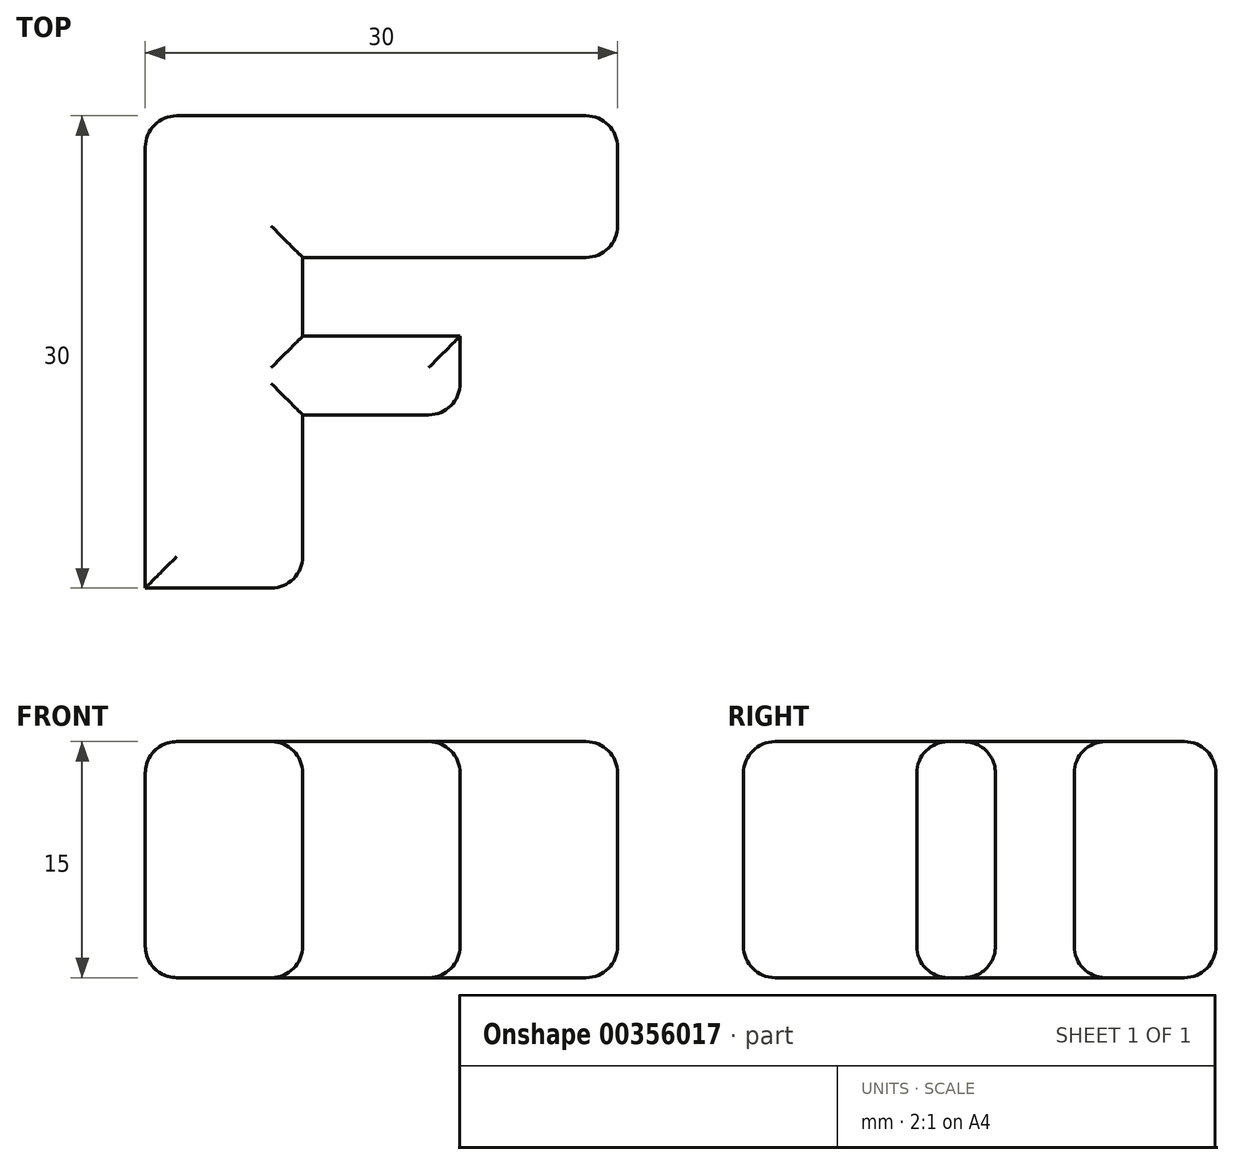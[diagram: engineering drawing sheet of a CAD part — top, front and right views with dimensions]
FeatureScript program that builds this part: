
annotation { "Feature Type Name" : "Feature", "Feature Type Description" : "" }
export const myFeature = defineFeature(function(context is Context, id is Id, definition is map)
    precondition{}
    {
        {
            var Q0;
            Q0=qCreatedBy(makeId("Top.planeOp"),FACE);
            var sketch = newSketch(context, id + "F0", { "sketchPlane" : qUnion([Q0])});
            skLineSegment(sketch, "E0", {"start": v(0, 0) * mm, "end": v(0, 30) * mm});
            skLineSegment(sketch, "E1", {"start": v(0, 30) * mm, "end": v(30, 30) * mm});
            skLineSegment(sketch, "E2", {"start": v(30, 30) * mm, "end": v(30, 21) * mm});
            skLineSegment(sketch, "E3", {"start": v(10, 21) * mm, "end": v(30, 21) * mm});
            skLineSegment(sketch, "E4", {"start": v(10, 21) * mm, "end": v(10, 16) * mm});
            skLineSegment(sketch, "E5", {"start": v(10, 16) * mm, "end": v(20, 16) * mm});
            skPoint(sketch, "E5.endSnap0", {"position": v(20, 21) * mm});
            skLineSegment(sketch, "E6", {"start": v(20, 16) * mm, "end": v(20, 11) * mm});
            skLineSegment(sketch, "E7", {"start": v(20, 11) * mm, "end": v(10, 11) * mm});
            skLineSegment(sketch, "E8", {"start": v(10, 11) * mm, "end": v(10, 0) * mm});
            skLineSegment(sketch, "E9", {"start": v(0, 0) * mm, "end": v(10, 0) * mm});
            skSolve(sketch);
        }
        {
            var Q0;
            Q0=makeQuery(id+"F0.imprint","IMPRINT",FACE,{"disambiguationData":[TD([[makeQuery(id+"F0.imprint","IMPRINT",EDGE,{"derivedFrom":sQuery(id+"F0.wireOp",EDGE,"E0")}),-1.0]])]});
            extrude(context, id + "F1", {"entities" : qUnion([Q0]), "depth" : 15 * mm});
        }
        {
            var Q0;
            Q0=makeQuery(id+"F1.opExtrude","SWEPT_FACE",FACE,{"disambiguationData":[OSD([sQuery(id+"F0.wireOp",EDGE,"E2")])]});
            var Q1;
            Q1=makeQuery(id+"F1.opExtrude","SWEPT_EDGE",EDGE,{"disambiguationData":[OSD([sQuery(id+"F0.wireOp",EDGE,"E6"),sQuery(id+"F0.wireOp",EDGE,"E7")])]});
            var Q2;
            Q2=makeQuery(id+"F1.opExtrude","SWEPT_EDGE",EDGE,{"disambiguationData":[OSD([sQuery(id+"F0.wireOp",EDGE,"E8"),sQuery(id+"F0.wireOp",EDGE,"E9")])]});
            var Q3;
            Q3=makeQuery(id+"F1.opExtrude","CAP_EDGE",EDGE,{"disambiguationData":[OSD([sQuery(id+"F0.wireOp",EDGE,"E3")])],"isStart":true});
            var Q4;
            Q4=makeQuery(id+"F1.opExtrude","CAP_EDGE",EDGE,{"disambiguationData":[OSD([sQuery(id+"F0.wireOp",EDGE,"E1")])],"isStart":false});
            var Q5;
            Q5=makeQuery(id+"F1.opExtrude","CAP_FACE",FACE,{"disambiguationData":[OSD([sQuery(id+"F0.wireOp",EDGE,"E0"),sQuery(id+"F0.wireOp",EDGE,"E1"),sQuery(id+"F0.wireOp",EDGE,"E2"),sQuery(id+"F0.wireOp",EDGE,"E3"),sQuery(id+"F0.wireOp",EDGE,"E4"),sQuery(id+"F0.wireOp",EDGE,"E5"),sQuery(id+"F0.wireOp",EDGE,"E6"),sQuery(id+"F0.wireOp",EDGE,"E7"),sQuery(id+"F0.wireOp",EDGE,"E8"),sQuery(id+"F0.wireOp",EDGE,"E9")])],"isStart":true});
            var Q6;
            Q6=makeQuery(id+"F1.opExtrude","SWEPT_FACE",FACE,{"disambiguationData":[OSD([sQuery(id+"F0.wireOp",EDGE,"E1")])]});
            var Q7;
            Q7=makeQuery(id+"F1.opExtrude","CAP_FACE",FACE,{"disambiguationData":[OSD([sQuery(id+"F0.wireOp",EDGE,"E0"),sQuery(id+"F0.wireOp",EDGE,"E1"),sQuery(id+"F0.wireOp",EDGE,"E2"),sQuery(id+"F0.wireOp",EDGE,"E3"),sQuery(id+"F0.wireOp",EDGE,"E4"),sQuery(id+"F0.wireOp",EDGE,"E5"),sQuery(id+"F0.wireOp",EDGE,"E6"),sQuery(id+"F0.wireOp",EDGE,"E7"),sQuery(id+"F0.wireOp",EDGE,"E8"),sQuery(id+"F0.wireOp",EDGE,"E9")])],"isStart":false});
            var Q8;
            Q8=makeQuery(id+"F1.opExtrude","CAP_EDGE",EDGE,{"disambiguationData":[OSD([sQuery(id+"F0.wireOp",EDGE,"E7")])],"isStart":true});
            fillet(context, id + "F2", {"entities" : qUnion([Q0, Q1, Q2, Q3, Q4, Q5, Q6, Q7, Q8]), "radius" : 2 * mm, "tangentPropagation" : true, "allowEdgeOverflow" : false});
        }
    });
